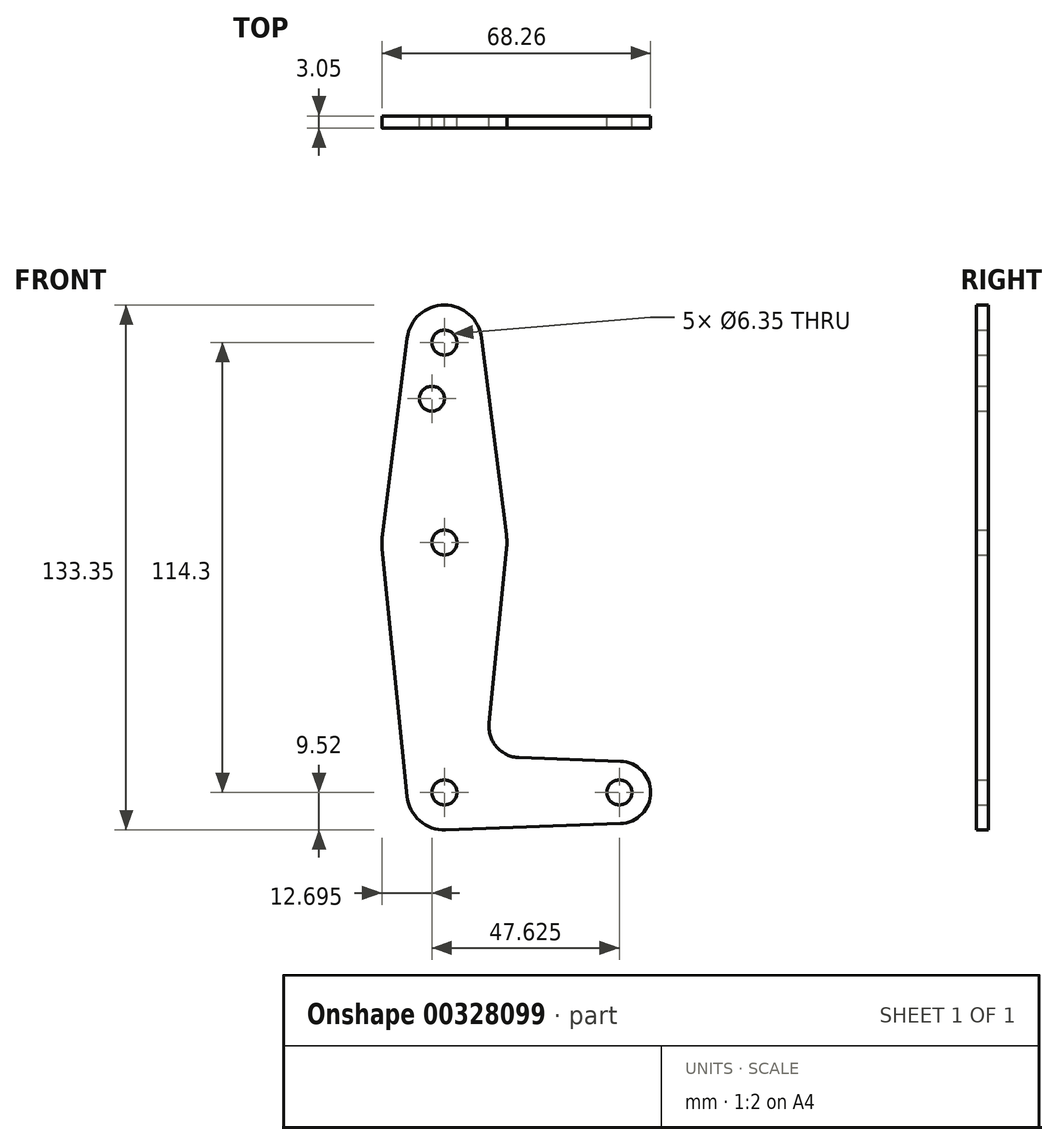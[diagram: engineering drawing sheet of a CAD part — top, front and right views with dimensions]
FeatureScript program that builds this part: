
annotation { "Feature Type Name" : "Feature", "Feature Type Description" : "" }
export const myFeature = defineFeature(function(context is Context, id is Id, definition is map)
    precondition{}
    {
        {
            var Q0;
            Q0=qCreatedBy(makeId("Front.planeOp"),FACE);
            var sketch = newSketch(context, id + "F0", { "sketchPlane" : qUnion([Q0])});
            skLineSegment(sketch, "E0", {"start": v(0, 0) * mm, "end": v(0, 114.3) * mm, "construction": true});
            skLineSegment(sketch, "E1", {"start": v(0, 0) * mm, "end": v(44.45, 0) * mm, "construction": true});
            skCircle(sketch, "E2", {"center": v(0, 114.3) * mm, "radius": 9.53 * mm});
            skCircle(sketch, "E3", {"center": v(0, 63.5) * mm, "radius": 15.88 * mm});
            skCircle(sketch, "E4", {"center": v(44.45, 0) * mm, "radius": 7.94 * mm});
            skLineSegment(sketch, "E5", {"start": v(-9.45, 115.5) * mm, "end": v(-15.75, 65.48) * mm});
            skLineSegment(sketch, "E6", {"start": v(9.45, 115.5) * mm, "end": v(15.75, 65.48) * mm});
            skCircle(sketch, "E7", {"center": v(0, 0) * mm, "radius": 9.53 * mm});
            skLineSegment(sketch, "E8", {"start": v(18.97, 8.85) * mm, "end": v(44.73, 7.93) * mm});
            skLineSegment(sketch, "E9", {"start": v(0.34, -9.52) * mm, "end": v(44.73, -7.93) * mm});
            skLineSegment(sketch, "E10", {"start": v(-15.8, 61.91) * mm, "end": v(-9.48, -0.95) * mm});
            skLineSegment(sketch, "E11", {"start": v(15.8, 61.91) * mm, "end": v(11.34, 17.6) * mm});
            skCircle(sketch, "E12", {"center": v(0, 114.3) * mm, "radius": 3.18 * mm});
            skCircle(sketch, "E13", {"center": v(0, 63.5) * mm, "radius": 3.18 * mm});
            skCircle(sketch, "E14", {"center": v(0, 0) * mm, "radius": 3.18 * mm});
            skCircle(sketch, "E15", {"center": v(44.45, 0) * mm, "radius": 3.18 * mm});
            skCircle(sketch, "E16", {"center": v(-3.18, 100.03) * mm, "radius": 3.18 * mm});
            skPoint(sketch, "E17.newPointA", {"position": v(9.48, -0.95) * mm});
            skPoint(sketch, "E17.newPointB", {"position": v(0.34, 9.52) * mm});
            skArc(sketch, "E17.filletArc", {"start": v(11.34, 17.6) * mm, "mid": v(13.26, 11.57) * mm, "end": v(18.97, 8.85) * mm});
            skSolve(sketch);
        }
        {
            var Q0;
            Q0 = qSketchRegion(id + "F0", true);
            extrude(context, id + "F1", {"entities" : qUnion([Q0]), "depth" : 3.05 * mm});
        }
    });
